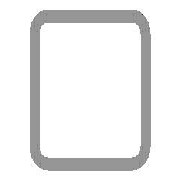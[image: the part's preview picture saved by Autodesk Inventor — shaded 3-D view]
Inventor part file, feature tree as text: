
AUTODESK INVENTOR PART (.ipt)
format: ipt  version: 2025 (Build 290162010, 162A)  size: 135,680 bytes
history: native  units: mm (DEFAULTED — no unit token found)
features: other x4, sketch x1, plane x1
ambient origin geometry x8: Origin, YZ Plane, XZ Plane, XY Plane, X Axis, Y Axis, Z Axis, Center Point
bodies: Solid1 (feature_tree), Body (feature_tree)
feature tree (6):
  parser-record x1  (decoder bookkeeping rows leaked as tree rows — omitted from the tree; the rows remain in map.json)
  other  "Driven Length"
  other  "Start Plane"
  other  "End Plane"
  sketch  "Sketch3"  dims[d3=2050.0mm d4=0.0mm d7=4.0mm d9=40.0mm d11=40.0mm d12=2.0mm d13=-0.0mm d14=2050.0mm d15=20.0mm d16=20.0mm d17=90.0deg d18=2050.0mm]
  plane  "Work Plane3"
